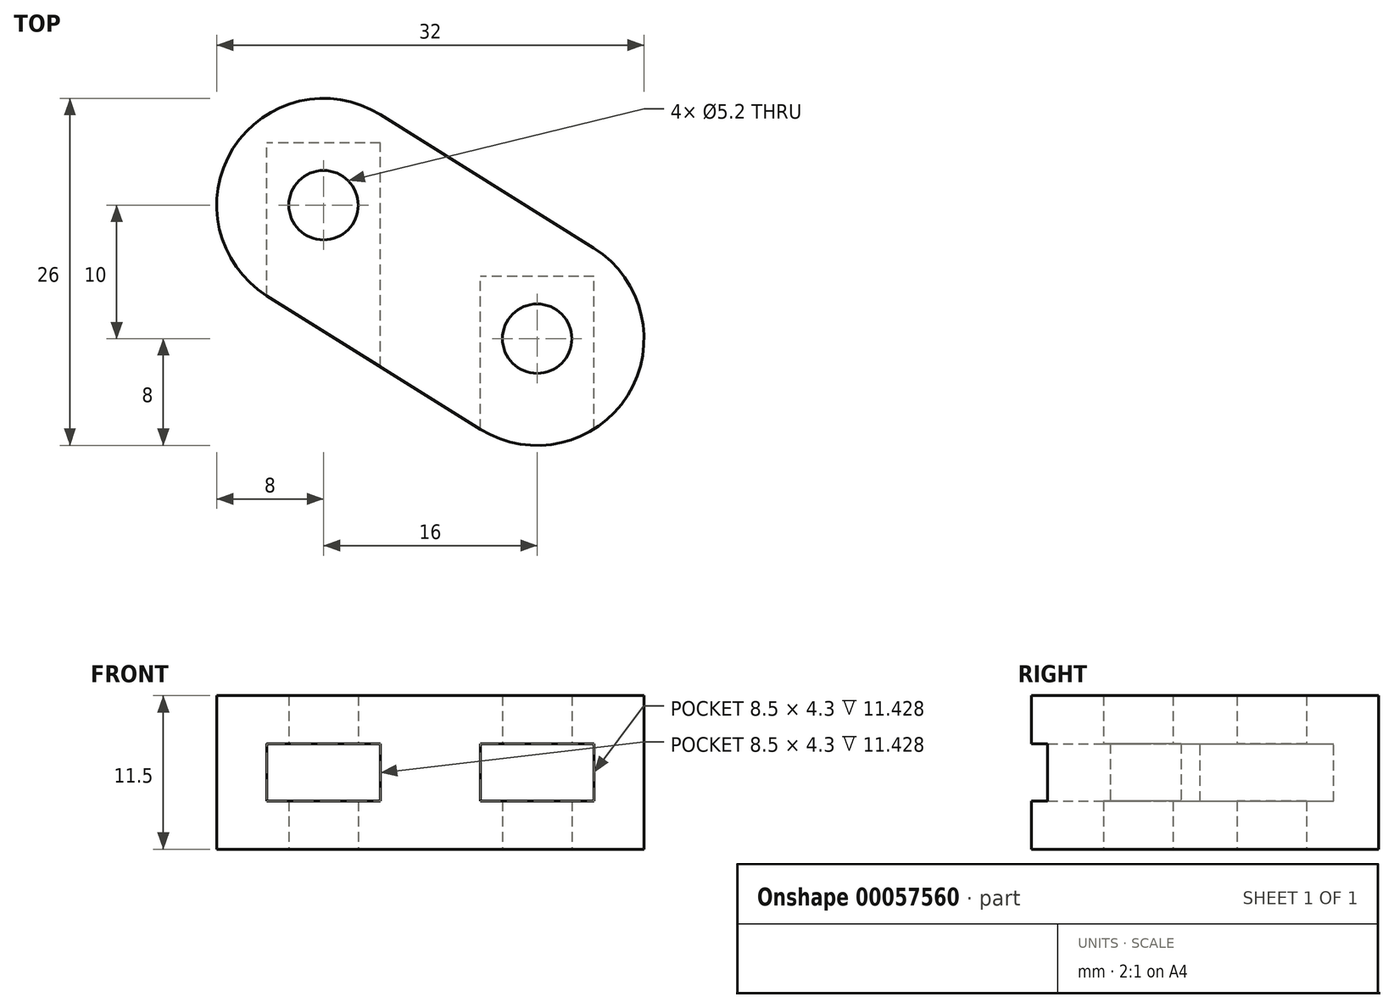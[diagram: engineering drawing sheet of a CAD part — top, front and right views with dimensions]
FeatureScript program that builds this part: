
annotation { "Feature Type Name" : "Feature", "Feature Type Description" : "" }
export const myFeature = defineFeature(function(context is Context, id is Id, definition is map)
    precondition{}
    {
        {
            var Q0;
            Q0=qCreatedBy(makeId("Top.planeOp"),FACE);
            var sketch = newSketch(context, id + "F0", { "sketchPlane" : qUnion([Q0])});
            skCircle(sketch, "E0", {"center": v(0, 0) * mm, "radius": 8 * mm});
            skCircle(sketch, "E1", {"center": v(16, -10) * mm, "radius": 8 * mm});
            skLineSegment(sketch, "E2", {"start": v(8, 0) * mm, "end": v(8, -10) * mm, "construction": true});
            skLineSegment(sketch, "E3", {"start": v(-4.24, -6.78) * mm, "end": v(11.76, -16.78) * mm});
            skLineSegment(sketch, "E4", {"start": v(4.24, 6.78) * mm, "end": v(20.24, -3.22) * mm});
            skCircle(sketch, "E5", {"center": v(0, 0) * mm, "radius": 2.6 * mm});
            skCircle(sketch, "E6", {"center": v(16, -10) * mm, "radius": 2.6 * mm});
            skSolve(sketch);
        }
        {
            var Q0;
            Q0=makeQuery(id+"F0.imprint","IMPRINT",FACE,{"disambiguationData":[TD([[makeQuery(id+"F0.imprint","IMPRINT",EDGE,{"derivedFrom":sQuery(id+"F0.wireOp",EDGE,"E5")}),-1.0]])]});
            var Q1;
            {var subQ0=sQuery(id+"F0.wireOp",EDGE,"E3");Q1=makeQuery(id+"F0.imprint","IMPRINT",FACE,{"disambiguationData":[TD([[makeQuery(id+"F0.imprint","IMPRINT",EDGE,{"derivedFrom":subQ0}),1.0]])]});}
            var Q2;
            Q2=makeQuery(id+"F0.imprint","IMPRINT",FACE,{"disambiguationData":[TD([[makeQuery(id+"F0.imprint","IMPRINT",EDGE,{"derivedFrom":sQuery(id+"F0.wireOp",EDGE,"E6")}),-1.0]])]});
            extrude(context, id + "F1", {"entities" : qUnion([Q0, Q1, Q2]), "depth" : 11.5 * mm});
        }
        {
            var Q0;
            Q0=makeQuery(id+"F1.opExtrude","CAP_FACE",FACE,{"disambiguationData":[OSD([sQuery(id+"F0.wireOp",EDGE,"E0"),sQuery(id+"F0.wireOp",EDGE,"E1"),sQuery(id+"F0.wireOp",EDGE,"E3"),sQuery(id+"F0.wireOp",EDGE,"E4"),sQuery(id+"F0.wireOp",EDGE,"E5"),sQuery(id+"F0.wireOp",EDGE,"E6")])],"isStart":false});
            var Q1;
            Q1=makeQuery(id+"F1.opExtrude","CAP_FACE",FACE,{"disambiguationData":[OSD([sQuery(id+"F0.wireOp",EDGE,"E0"),sQuery(id+"F0.wireOp",EDGE,"E1"),sQuery(id+"F0.wireOp",EDGE,"E3"),sQuery(id+"F0.wireOp",EDGE,"E4"),sQuery(id+"F0.wireOp",EDGE,"E5"),sQuery(id+"F0.wireOp",EDGE,"E6")])],"isStart":true});
            cPlane(context, id + "F2", {"entities" : qUnion([Q0, Q1]), "cplaneType" : CPlaneType.MID_PLANE, "offset" : 150 * mm, "width" : 150 * mm, "height" : 150 * mm});
        }
        {
            var Q0;
            Q0=qCreatedBy(id+"F2.planeOp",FACE);
            var sketch = newSketch(context, id + "F3", { "sketchPlane" : qUnion([Q0])});
            skLineSegment(sketch, "E7.rect.bottom", {"start": v(4.25, -4.65) * mm, "end": v(-4.25, -4.65) * mm});
            skLineSegment(sketch, "E7.rect.top", {"start": v(4.25, 4.65) * mm, "end": v(-4.25, 4.65) * mm});
            skLineSegment(sketch, "E7.rect.left", {"start": v(4.25, -4.65) * mm, "end": v(4.25, 4.65) * mm});
            skLineSegment(sketch, "E7.rect.right", {"start": v(-4.25, -4.65) * mm, "end": v(-4.25, 4.65) * mm});
            skPoint(sketch, "E7.rect.middle", {"position": v(0, 0) * mm});
            skLineSegment(sketch, "E8.bottom", {"start": v(-4.25, -4.65) * mm, "end": v(4.25, -4.65) * mm});
            skLineSegment(sketch, "E8.top", {"start": v(-4.25, -14.65) * mm, "end": v(4.25, -14.65) * mm});
            skLineSegment(sketch, "E8.left", {"start": v(-4.25, -4.65) * mm, "end": v(-4.25, -14.65) * mm});
            skLineSegment(sketch, "E8.right", {"start": v(4.25, -4.65) * mm, "end": v(4.25, -14.65) * mm});
            skLineSegment(sketch, "E9.rect.bottom", {"start": v(20.25, -14.65) * mm, "end": v(11.75, -14.65) * mm});
            skLineSegment(sketch, "E9.rect.top", {"start": v(20.25, -5.35) * mm, "end": v(11.75, -5.35) * mm});
            skLineSegment(sketch, "E9.rect.left", {"start": v(20.25, -14.65) * mm, "end": v(20.25, -5.35) * mm});
            skLineSegment(sketch, "E9.rect.right", {"start": v(11.75, -14.65) * mm, "end": v(11.75, -5.35) * mm});
            skPoint(sketch, "E9.rect.middle", {"position": v(16, -10) * mm});
            skLineSegment(sketch, "E10.bottom", {"start": v(11.75, -14.65) * mm, "end": v(20.25, -14.65) * mm});
            skLineSegment(sketch, "E10.top", {"start": v(11.75, -24.65) * mm, "end": v(20.25, -24.65) * mm});
            skLineSegment(sketch, "E10.left", {"start": v(11.75, -14.65) * mm, "end": v(11.75, -24.65) * mm});
            skLineSegment(sketch, "E10.right", {"start": v(20.25, -14.65) * mm, "end": v(20.25, -24.65) * mm});
            skSolve(sketch);
        }
        {
            var Q0;
            Q0 = qSketchRegion(id + "F3", true);
            extrude(context, id + "F4", {"entities" : qUnion([Q0]), "operationType" : NewBodyOperationType.REMOVE, "endBound" : BoundingType.SYMMETRIC, "oppositeDirection" : true, "depth" : 4.3 * mm});
        }
    });
